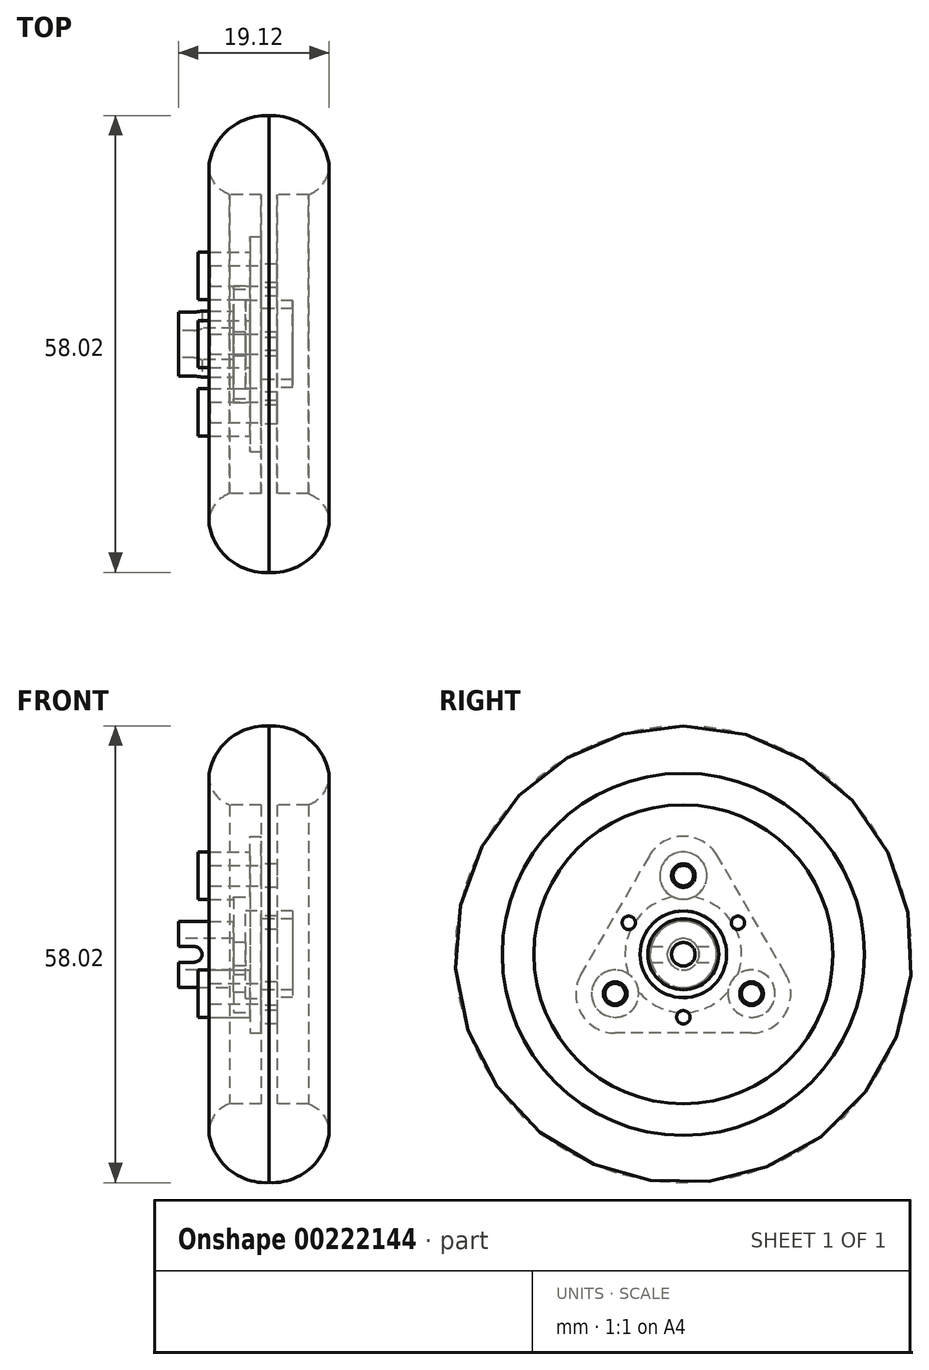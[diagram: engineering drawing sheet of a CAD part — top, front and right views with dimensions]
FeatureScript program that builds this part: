
annotation { "Feature Type Name" : "Feature", "Feature Type Description" : "" }
export const myFeature = defineFeature(function(context is Context, id is Id, definition is map)
    precondition{}
    {
        {
            var Q0;
            Q0=qCreatedBy(makeId("Front.planeOp"),FACE);
            var sketch = newSketch(context, id + "F0", { "sketchPlane" : qUnion([Q0])});
            skCircle(sketch, "E0", {"center": v(0, 0) * mm, "radius": 4.5 * mm, "construction": true});
            skCircle(sketch, "E1", {"center": v(0, 0) * mm, "radius": 5.5 * mm, "construction": true});
            skCircle(sketch, "E2", {"center": v(0, 0) * mm, "radius": 19 * mm, "construction": true});
            skCircle(sketch, "E3", {"center": v(0, 0) * mm, "radius": 23 * mm, "construction": true});
            skCircle(sketch, "E4", {"center": v(0, 0) * mm, "radius": 29 * mm, "construction": true});
            skLineSegment(sketch, "E5.bottom", {"start": v(0, 4.5) * mm, "end": v(1, 4.5) * mm});
            skLineSegment(sketch, "E5.left", {"start": v(0, 4.5) * mm, "end": v(0, 19) * mm});
            skLineSegment(sketch, "E5.right", {"start": v(1, 4.5) * mm, "end": v(1, 19) * mm});
            skLineSegment(sketch, "E6.bottom", {"start": v(0, 4.5) * mm, "end": v(3, 4.5) * mm});
            skLineSegment(sketch, "E6.top", {"start": v(0, 5.5) * mm, "end": v(3, 5.5) * mm});
            skLineSegment(sketch, "E6.left", {"start": v(0, 4.5) * mm, "end": v(0, 5.5) * mm});
            skLineSegment(sketch, "E6.right", {"start": v(3, 4.5) * mm, "end": v(3, 5.5) * mm});
            skLineSegment(sketch, "E7.bottom", {"start": v(0, 23) * mm, "end": v(5, 23) * mm});
            skLineSegment(sketch, "E7.top", {"start": v(0, 19) * mm, "end": v(5, 19) * mm});
            skLineSegment(sketch, "E7.left", {"start": v(0, 23) * mm, "end": v(0, 19) * mm});
            skLineSegment(sketch, "E7.right", {"start": v(5, 23) * mm, "end": v(5, 19) * mm});
            skCircle(sketch, "E8", {"center": v(0, 23) * mm, "radius": 7.6 * mm, "construction": true});
            skArc(sketch, "E9", {"start": v(5, 19) * mm, "mid": v(7, 20.55) * mm, "end": v(7.6, 23) * mm});
            skArc(sketch, "E10", {"start": v(7.6, 23) * mm, "mid": v(4.94, 27.44) * mm, "end": v(0, 29) * mm});
            skLineSegment(sketch, "E11.MirrorCS", {"start": v(0, 4.5) * mm, "end": v(-1, 4.5) * mm});
            skLineSegment(sketch, "E12.MirrorCS", {"start": v(0, 5.5) * mm, "end": v(-3, 5.5) * mm});
            skLineSegment(sketch, "E13.MirrorCS", {"start": v(-3, 4.5) * mm, "end": v(-3, 5.5) * mm});
            skLineSegment(sketch, "E14.MirrorCS", {"start": v(0, 4.5) * mm, "end": v(-3, 4.5) * mm});
            skLineSegment(sketch, "E15.MirrorCS", {"start": v(0, 19) * mm, "end": v(-5, 19) * mm});
            skArc(sketch, "E16.MirrorCS", {"start": v(-5, 19) * mm, "mid": v(-7, 20.55) * mm, "end": v(-7.6, 23) * mm});
            skLineSegment(sketch, "E17.MirrorCS", {"start": v(-5, 23) * mm, "end": v(-5, 19) * mm});
            skArc(sketch, "E18.MirrorCS", {"start": v(-7.6, 23) * mm, "mid": v(-4.94, 27.44) * mm, "end": v(0, 29) * mm});
            skLineSegment(sketch, "E19.MirrorCS", {"start": v(-1, 4.5) * mm, "end": v(-1, 19) * mm});
            skLineSegment(sketch, "E20.MirrorCS", {"start": v(0, 23) * mm, "end": v(-5, 23) * mm});
            skSolve(sketch);
        }
        {
            var Q0;
            Q0=qCreatedBy(makeId("Front.planeOp"),FACE);
            var sketch = newSketch(context, id + "F1", { "sketchPlane" : qUnion([Q0])});
            skLineSegment(sketch, "E21", {"start": v(-37.16, 0) * mm, "end": v(45.3, 0) * mm, "construction": true});
            skSolve(sketch);
        }
        {
            var Q0;
            Q0 = qSketchRegion(id + "F0", true);
            var Q1;
            Q1=sQuery(id+"F1.wireOp",EDGE,"E21");
            revolve(context, id + "F2", {"entities" : qUnion([Q0]), "axis" : qUnion([Q1]), "revolveType" : RevolveType.FULL});
        }
        {
            var Q0;
            Q0=makeQuery(id+"F2.opRevolve","SWEPT_FACE",FACE,{"disambiguationData":[OSD([sQuery(id+"F0.wireOp",EDGE,"E19.MirrorCS")])]});
            var sketch = newSketch(context, id + "F3", { "sketchPlane" : qUnion([Q0])});
            skCircle(sketch, "E22", {"center": v(0, 0) * mm, "radius": 10 * mm, "construction": true});
            skCircle(sketch, "E23", {"center": v(0, 10) * mm, "radius": 1.5 * mm});
            skCircle(sketch, "E24.1.0", {"center": v(-8.66, -5) * mm, "radius": 1.5 * mm});
            skCircle(sketch, "E24.2.0", {"center": v(8.66, -5) * mm, "radius": 1.5 * mm});
            skCircle(sketch, "E25", {"center": v(0, 0) * mm, "radius": 8 * mm, "construction": true});
            skCircle(sketch, "E26", {"center": v(0, -8) * mm, "radius": 0.85 * mm});
            skCircle(sketch, "E27.1.0", {"center": v(6.93, 4) * mm, "radius": 0.85 * mm});
            skCircle(sketch, "E27.2.0", {"center": v(-6.93, 4) * mm, "radius": 0.85 * mm});
            skSolve(sketch);
        }
        {
            var Q0;
            Q0 = qSketchRegion(id + "F3", true);
            extrude(context, id + "F4", {"entities" : qUnion([Q0]), "operationType" : NewBodyOperationType.REMOVE, "endBound" : BoundingType.THROUGH_ALL, "oppositeDirection" : true, "depth" : 25 * mm});
        }
        {
            var Q0;
            Q0=makeQuery(id+"F2.opRevolve","SWEPT_FACE",FACE,{"disambiguationData":[OSD([sQuery(id+"F0.wireOp",EDGE,"E19.MirrorCS")])]});
            var sketch = newSketch(context, id + "F5", { "sketchPlane" : qUnion([Q0])});
            skLineSegment(sketch, "E28", {"start": v(0, 10) * mm, "end": v(-8.66, -5) * mm, "construction": true});
            skLineSegment(sketch, "E29", {"start": v(-8.66, -5) * mm, "end": v(8.66, -5) * mm, "construction": true});
            skLineSegment(sketch, "E30", {"start": v(8.66, -5) * mm, "end": v(0, 10) * mm, "construction": true});
            skLineSegment(sketch, "E31", {"start": v(-14.43, -5) * mm, "end": v(-3.32, 14.25) * mm, "construction": true});
            skLineSegment(sketch, "E32", {"start": v(2.44, 15.78) * mm, "end": v(14.43, -5) * mm, "construction": true});
            skLineSegment(sketch, "E33", {"start": v(-13.1, -10) * mm, "end": v(12.36, -10) * mm, "construction": true});
            skCircle(sketch, "E34", {"center": v(0, 10) * mm, "radius": 5 * mm});
            skCircle(sketch, "E35", {"center": v(-8.66, -5) * mm, "radius": 5 * mm});
            skCircle(sketch, "E36", {"center": v(8.66, -5) * mm, "radius": 5 * mm});
            skLineSegment(sketch, "E37", {"start": v(-13, -2.5) * mm, "end": v(-4.33, 12.5) * mm});
            skLineSegment(sketch, "E38", {"start": v(4.33, 12.5) * mm, "end": v(13, -2.5) * mm});
            skLineSegment(sketch, "E39", {"start": v(-8.66, -10) * mm, "end": v(8.66, -10) * mm});
            skSolve(sketch);
        }
        {
            var Q0;
            Q0 = qSketchRegion(id + "F5", true);
            extrude(context, id + "F6", {"entities" : qUnion([Q0]), "depth" : 1.4 * mm});
        }
        {
            var Q0;
            Q0=makeQuery(id+"F6.opExtrude","CAP_FACE",FACE,{"disambiguationData":[OSD([sQuery(id+"F5.wireOp",EDGE,"E34"),sQuery(id+"F5.wireOp",EDGE,"E35"),sQuery(id+"F5.wireOp",EDGE,"E36"),sQuery(id+"F5.wireOp",EDGE,"E37"),sQuery(id+"F5.wireOp",EDGE,"E38"),sQuery(id+"F5.wireOp",EDGE,"E39")])],"isStart":true});
            var sketch = newSketch(context, id + "F7", { "sketchPlane" : qUnion([Q0])});
            skCircle(sketch, "E40", {"center": v(0, 10) * mm, "radius": 3 * mm});
            skCircle(sketch, "E41.1.0", {"center": v(-8.66, -5) * mm, "radius": 3 * mm});
            skCircle(sketch, "E41.2.0", {"center": v(8.66, -5) * mm, "radius": 3 * mm});
            skPoint(sketch, "E41.center", {"position": v(0, 0) * mm});
            skSolve(sketch);
        }
        {
            var Q0;
            Q0 = qSketchRegion(id + "F7", true);
            extrude(context, id + "F8", {"entities" : qUnion([Q0]), "operationType" : NewBodyOperationType.ADD, "oppositeDirection" : true, "depth" : 8 * mm});
        }
        {
            var Q0;
            Q0=makeQuery(id+"F6.opExtrude","CAP_FACE",FACE,{"disambiguationData":[OSD([sQuery(id+"F5.wireOp",EDGE,"E34"),sQuery(id+"F5.wireOp",EDGE,"E35"),sQuery(id+"F5.wireOp",EDGE,"E36"),sQuery(id+"F5.wireOp",EDGE,"E37"),sQuery(id+"F5.wireOp",EDGE,"E38"),sQuery(id+"F5.wireOp",EDGE,"E39")])],"isStart":true});
            var sketch = newSketch(context, id + "F9", { "sketchPlane" : qUnion([Q0])});
            skCircle(sketch, "E42", {"center": v(0, 0) * mm, "radius": 4.2 * mm});
            skSolve(sketch);
        }
        {
            var Q0;
            Q0 = qSketchRegion(id + "F9", true);
            extrude(context, id + "F10", {"entities" : qUnion([Q0]), "operationType" : NewBodyOperationType.ADD, "oppositeDirection" : true, "depth" : 10.5 * mm});
        }
        {
            var Q0;
            Q0=makeQuery(id+"F6.opExtrude","CAP_FACE",FACE,{"disambiguationData":[OSD([sQuery(id+"F5.wireOp",EDGE,"E34"),sQuery(id+"F5.wireOp",EDGE,"E35"),sQuery(id+"F5.wireOp",EDGE,"E36"),sQuery(id+"F5.wireOp",EDGE,"E37"),sQuery(id+"F5.wireOp",EDGE,"E38"),sQuery(id+"F5.wireOp",EDGE,"E39")])],"isStart":true});
            var sketch = newSketch(context, id + "F11", { "sketchPlane" : qUnion([Q0])});
            skCircle(sketch, "E43", {"center": v(0, 0) * mm, "radius": 7.4 * mm});
            skSolve(sketch);
        }
        {
            var Q0;
            Q0 = qSketchRegion(id + "F11", true);
            extrude(context, id + "F12", {"entities" : qUnion([Q0]), "operationType" : NewBodyOperationType.ADD, "oppositeDirection" : true, "depth" : 3.5 * mm});
        }
        {
            var Q0;
            Q0=makeQuery(id+"F6.opExtrude","CAP_FACE",FACE,{"disambiguationData":[OSD([sQuery(id+"F5.wireOp",EDGE,"E34"),sQuery(id+"F5.wireOp",EDGE,"E35"),sQuery(id+"F5.wireOp",EDGE,"E36"),sQuery(id+"F5.wireOp",EDGE,"E37"),sQuery(id+"F5.wireOp",EDGE,"E38"),sQuery(id+"F5.wireOp",EDGE,"E39")])],"isStart":true});
            var sketch = newSketch(context, id + "F13", { "sketchPlane" : qUnion([Q0])});
            skCircle(sketch, "E44", {"center": v(0, 0) * mm, "radius": 5.6 * mm});
            skSolve(sketch);
        }
        {
            var Q0;
            Q0 = qSketchRegion(id + "F13", true);
            extrude(context, id + "F14", {"entities" : qUnion([Q0]), "operationType" : NewBodyOperationType.REMOVE, "oppositeDirection" : true, "depth" : 2 * mm});
        }
        {
            var Q0;
            Q0=makeQuery(id+"F10.opExtrude","CAP_FACE",FACE,{"disambiguationData":[OSD([sQuery(id+"F9.wireOp",EDGE,"E42")])],"isStart":false});
            var sketch = newSketch(context, id + "F15", { "sketchPlane" : qUnion([Q0])});
            skCircle(sketch, "E45", {"center": v(0, 0) * mm, "radius": 1.5 * mm});
            skSolve(sketch);
        }
        {
            var Q0;
            Q0 = qSketchRegion(id + "F15", true);
            extrude(context, id + "F16", {"entities" : qUnion([Q0]), "operationType" : NewBodyOperationType.REMOVE, "endBound" : BoundingType.THROUGH_ALL, "oppositeDirection" : true, "depth" : 25 * mm});
        }
        {
            var Q0;
            Q0=makeQuery(id+"F10.opExtrude","CAP_FACE",FACE,{"disambiguationData":[OSD([sQuery(id+"F9.wireOp",EDGE,"E42")])],"isStart":false});
            var sketch = newSketch(context, id + "F17", { "sketchPlane" : qUnion([Q0])});
            skCircle(sketch, "E46", {"center": v(0, 0) * mm, "radius": 2 * mm});
            skSolve(sketch);
        }
        {
            var Q0;
            Q0 = qSketchRegion(id + "F17", true);
            extrude(context, id + "F18", {"entities" : qUnion([Q0]), "operationType" : NewBodyOperationType.REMOVE, "oppositeDirection" : true, "depth" : 7 * mm});
        }
        {
            var Q0;
            Q0=makeQuery(id+"F6.opExtrude","CAP_FACE",FACE,{"disambiguationData":[OSD([sQuery(id+"F5.wireOp",EDGE,"E34"),sQuery(id+"F5.wireOp",EDGE,"E35"),sQuery(id+"F5.wireOp",EDGE,"E36"),sQuery(id+"F5.wireOp",EDGE,"E37"),sQuery(id+"F5.wireOp",EDGE,"E38"),sQuery(id+"F5.wireOp",EDGE,"E39")])],"isStart":true});
            var sketch = newSketch(context, id + "F19", { "sketchPlane" : qUnion([Q0])});
            skCircle(sketch, "E47", {"center": v(0, 10) * mm, "radius": 1.3 * mm});
            skCircle(sketch, "E48.1.0", {"center": v(-8.66, -5) * mm, "radius": 1.3 * mm});
            skCircle(sketch, "E48.2.0", {"center": v(8.66, -5) * mm, "radius": 1.3 * mm});
            skPoint(sketch, "E48.center", {"position": v(0, 0) * mm});
            skSolve(sketch);
        }
        {
            var Q0;
            Q0 = qSketchRegion(id + "F19", true);
            extrude(context, id + "F20", {"entities" : qUnion([Q0]), "operationType" : NewBodyOperationType.REMOVE, "oppositeDirection" : true, "depth" : 6.5 * mm});
        }
        {
            var Q0;
            Q0=qCreatedBy(makeId("Front.planeOp"),FACE);
            var sketch = newSketch(context, id + "F21", { "sketchPlane" : qUnion([Q0])});
            skCircle(sketch, "E49", {"center": v(-11.5, 0) * mm, "radius": 1 * mm, "construction": true});
            skLineSegment(sketch, "E50.bottom", {"start": v(-11.5, -1) * mm, "end": v(-9.5, -1) * mm});
            skLineSegment(sketch, "E50.top", {"start": v(-11.5, 1) * mm, "end": v(-9.5, 1) * mm});
            skLineSegment(sketch, "E50.left", {"start": v(-11.5, -1) * mm, "end": v(-11.5, 1) * mm});
            skArc(sketch, "E51", {"start": v(-9.5, 1) * mm, "mid": v(-8.5, 0) * mm, "end": v(-9.5, -1) * mm});
            skSolve(sketch);
        }
        {
            var Q0;
            Q0 = qSketchRegion(id + "F21", true);
            extrude(context, id + "F22", {"entities" : qUnion([Q0]), "operationType" : NewBodyOperationType.REMOVE, "oppositeDirection" : true, "depth" : 25 * mm, "hasSecondDirection" : true, "secondDirectionOppositeDirection" : false, "secondDirectionDepth" : 25 * mm});
        }
    });
